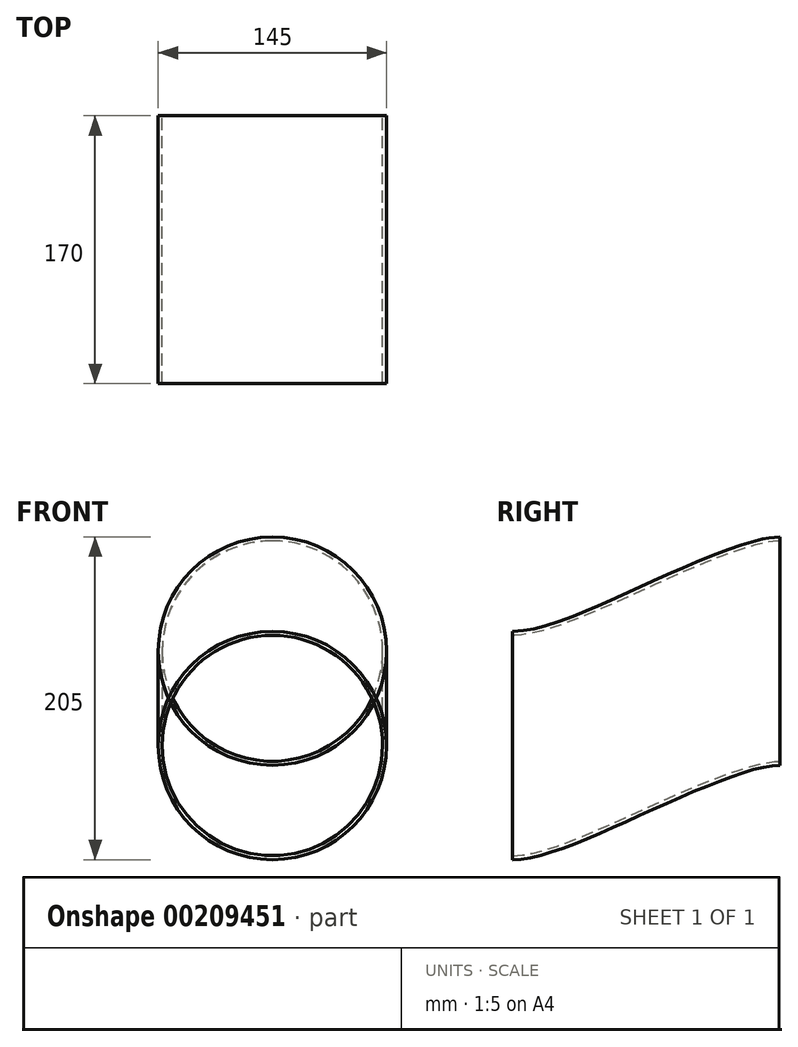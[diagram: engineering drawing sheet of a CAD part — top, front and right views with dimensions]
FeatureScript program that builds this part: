
annotation { "Feature Type Name" : "Feature", "Feature Type Description" : "" }
export const myFeature = defineFeature(function(context is Context, id is Id, definition is map)
    precondition{}
    {
        {
            var Q0;
            Q0=qCreatedBy(makeId("Right.planeOp"),FACE);
            var sketch = newSketch(context, id + "F0", { "sketchPlane" : qUnion([Q0])});
            skFitSpline(sketch, "E0", {"points": [v(0, 0) * mm, v(-85, -30) * mm, v(-170, -60) * mm], "startDerivative": vector(-105.04, 0) * mm, "endDerivative": vector(-121.15, 0) * mm});
            skLineSegment(sketch, "E1", {"start": v(0, 0) * mm, "end": v(22.7, 0) * mm, "construction": true});
            skLineSegment(sketch, "E2", {"start": v(-134.49, -60) * mm, "end": v(-170, -60) * mm, "construction": true});
            skSolve(sketch);
        }
        {
            var Q0;
            Q0=qCreatedBy(makeId("Front.planeOp"),FACE);
            var sketch = newSketch(context, id + "F1", { "sketchPlane" : qUnion([Q0])});
            skCircle(sketch, "E3", {"center": v(0, 0) * mm, "radius": 72.5 * mm});
            skSolve(sketch);
        }
        {
            var Q0;
            Q0=makeQuery(id+"F1.imprint","IMPRINT",FACE,{"disambiguationData":[TD([[makeQuery(id+"F1.imprint","IMPRINT",EDGE,{"derivedFrom":sQuery(id+"F1.wireOp",EDGE,"E3")}),1.0]])]});
            var Q1;
            Q1=sQuery(id+"F0.wireOp",EDGE,"E0");
            sweep(context, id + "F2", {"profiles" : qUnion([Q0]), "path" : qUnion([Q1]), "keepProfileOrientation" : true});
        }
        {
            var Q0;
            Q0=makeQuery(id+"F2.opSweep","CAP_FACE",FACE,{"disambiguationData":[OSD([sQuery(id+"F0.wireOp",VERTEX,"E0.start"),sQuery(id+"F1.wireOp",EDGE,"E3")])],"isStart":true});
            var Q1;
            Q1=makeQuery(id+"F2.opSweep","CAP_FACE",FACE,{"disambiguationData":[OSD([sQuery(id+"F0.wireOp",VERTEX,"E0.end"),sQuery(id+"F1.wireOp",EDGE,"E3")])],"isStart":false});
            shell(context, id + "F3", {"entities" : qUnion([Q0, Q1]), "thickness" : 2.5 * mm});
        }
    });
